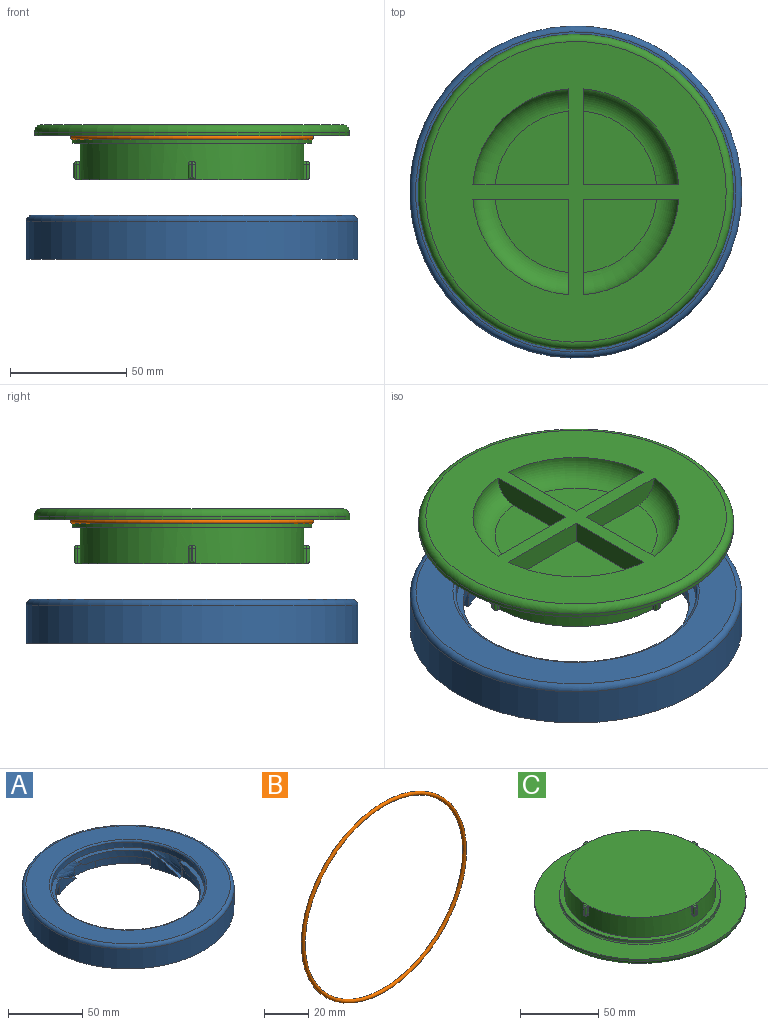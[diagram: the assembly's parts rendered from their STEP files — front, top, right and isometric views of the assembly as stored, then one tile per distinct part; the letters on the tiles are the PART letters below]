
ASSEMBLY  parts=3 mates=2
PART A: 46 faces, bbox 156.1x156.1x20.2 mm
  f0: plane 143.07x143.07mm, normal (0,0,-1), area 7927.9mm2, adj f7,f9,f11,f13,f15,f16,f18,f20
  f1: bspline ~17.63x13.21mm, area 24mm2, adj f10,f11,f17,f40
  f2: bspline ~17.63x13.21mm, area 24mm2, adj f8,f9,f19,f35
  f3: bspline ~17.63x13.21mm, area 24mm2, adj f6,f15,f21,f30
  f4: bspline ~17.63x13.21mm, area 24mm2, adj f5,f7,f23,f25
  f5: plane 46.03x29.1mm, normal (0,0,1), area 168.1mm2, adj f4,f7,f12,f16
  f6: plane 46.03x29.1mm, normal (0,0,1), area 168.1mm2, adj f3,f12,f15,f22
  f7: cylinder r=48.74mm len=48.74mm, axis (0,0,1), area 414.5mm2, adj f0,f4,f5,f16,f25,f28
  f8: plane 46.03x29.1mm, normal (0,0,1), area 168.1mm2, adj f2,f9,f12,f20
  f9: cylinder r=48.74mm len=48.74mm, axis (0,0,1), area 414.5mm2, adj f0,f2,f8,f20,f35,f36
  f10: plane 46.03x29.1mm, normal (0,0,1), area 168.1mm2, adj f1,f11,f12,f18
  f11: cylinder r=48.74mm len=48.74mm, axis (0,0,1), area 414.5mm2, adj f0,f1,f10,f18,f40,f41
  f12: cylinder r=51.82mm len=103.63mm, axis (0,0,-1), area 1447.2mm2, adj f5,f6,f8,f10,f17,f19,f21,f23
  f13: cylinder r=71.53mm len=143.07mm, axis (0,0,-1), area 7363.4mm2, adj f0,f44
  f14: plane 137.99x137.99mm, normal (0,0,1), area 6100.6mm2, adj f44,f45
  f15: cylinder r=48.74mm len=48.74mm, axis (0,0,1), area 414.5mm2, adj f0,f3,f6,f22,f30,f31
  f16: bspline ~24.16x13.21mm, area 56.9mm2, adj f0,f5,f7,f17
  f17: bspline ~41.8x13.21mm, area 183.8mm2, adj f1,f12,f16,f39,f40
  f18: bspline ~24.16x13.21mm, area 56.9mm2, adj f0,f10,f11,f19
  f19: bspline ~41.8x13.21mm, area 183.8mm2, adj f2,f12,f18,f34,f35
  f20: bspline ~24.16x13.21mm, area 56.9mm2, adj f0,f8,f9,f21
  f21: bspline ~41.8x13.21mm, area 183.8mm2, adj f3,f12,f20,f29,f30
  f22: bspline ~24.16x13.21mm, area 56.9mm2, adj f0,f6,f15,f23
  f23: bspline ~41.8x13.21mm, area 183.8mm2, adj f4,f12,f22,f24,f25
  f24: plane 9.07x2.34mm, normal (1,0,0), area 6.6mm2, adj f23,f25,f26
  f25: plane 46.34x30.01mm, normal (0,0,-1), area 155.7mm2, adj f4,f7,f23,f24,f26,f27,f28
  f26: extruded ~17.63x7.82mm, area 140.8mm2, adj f0,f24,f25,f27
  f27: cylinder r=51.82mm len=28.7mm, axis (0,0,-1), area 307.9mm2, adj f0,f25,f26,f28
  f28: plane 7.82x2.75mm, normal (-0.45,0.89,0), area 24.1mm2, adj f0,f7,f25,f27
  f29: plane 9.07x2.34mm, normal (0,1,0), area 6.6mm2, adj f21,f30,f32
  f30: plane 46.34x30.01mm, normal (0,0,-1), area 155.7mm2, adj f3,f15,f21,f29,f31,f32,f33
  f31: plane 7.82x2.75mm, normal (-0.89,-0.45,0), area 24.1mm2, adj f0,f15,f30,f33
  f32: extruded ~17.63x7.82mm, area 140.8mm2, adj f0,f29,f30,f33
  f33: cylinder r=51.82mm len=28.7mm, axis (0,0,-1), area 307.9mm2, adj f0,f30,f31,f32
  f34: plane 9.07x2.34mm, normal (-1,0,0), area 6.6mm2, adj f19,f35,f37
  f35: plane 46.34x30.01mm, normal (0,0,-1), area 155.7mm2, adj f2,f9,f19,f34,f36,f37,f38
  f36: plane 7.82x2.75mm, normal (0.45,-0.89,0), area 24.1mm2, adj f0,f9,f35,f38
  f37: extruded ~17.63x7.82mm, area 140.8mm2, adj f0,f34,f35,f38
  f38: cylinder r=51.82mm len=28.7mm, axis (0,0,-1), area 307.9mm2, adj f0,f35,f36,f37
  f39: plane 9.07x2.34mm, normal (0,-1,0), area 6.6mm2, adj f17,f40,f42
  f40: plane 46.34x30.01mm, normal (0,0,-1), area 155.7mm2, adj f1,f11,f17,f39,f41,f42,f43
  f41: plane 7.82x2.75mm, normal (0.89,0.45,0), area 24.1mm2, adj f0,f11,f40,f43
  f42: extruded ~17.63x7.82mm, area 140.8mm2, adj f0,f39,f40,f43
  f43: cylinder r=51.82mm len=28.7mm, axis (0,0,-1), area 307.9mm2, adj f0,f40,f41,f42
  f44: torus R=68.99mm, axis (0,0,1), area 1770.1mm2, adj f13,f14
  f45: torus R=53.09mm, axis (0,0,1), area 655.3mm2, adj f12,f14
PART B: 1 faces, bbox 113.5x1.8x113.5 mm
  f0: torus R=51.55mm, axis (0,-1,0), area 1809.2mm2
PART C: 80 faces, bbox 147.5x147.5x30.9 mm
  f0: plane 129.54x129.54mm, normal (0,0,-1), area 8060mm2, adj f36,f37,f39,f40,f42,f43,f45,f46
  f1: cylinder r=51.59mm len=103.19mm, axis (0,0,-1), area 514.6mm2, adj f2,f5
  f2: plane 103.19x103.19mm, normal (0,0,1), area 1045.8mm2, adj f1,f4
  f3: plane 96.55x96.55mm, normal (0,0,1), area 7316.9mm2, adj f4,f14,f15,f28,f29
  f4: cylinder r=48.26mm len=96.52mm, axis (0,0,-1), area 4679.5mm2, adj f2,f3,f9,f10,f11,f12,f13,f16
  f5: torus R=51.59mm, axis (0,0,1), area 800.5mm2, adj f1,f7
  f6: cylinder r=67.95mm len=135.89mm, axis (0,0,-1), area 677.7mm2, adj f7,f52
  f7: plane 135.89x135.89mm, normal (0,0,1), area 6140.6mm2, adj f5,f6
  f8: plane 5.29x0.64mm, normal (0,-1,0), area 3.4mm2, adj f71,f74,f75,f76
  f9: plane 6.56x1.3mm, normal (1,0,0), area 8.5mm2, adj f4,f10,f14,f75
  f10: cylinder r=1.27mm len=1.3mm, axis (0,1,0), area 2.6mm2, adj f4,f9,f11,f73
  f11: plane 1.27x0.64mm, normal (0,0,-1), area 0.8mm2, adj f4,f10,f13,f71
  f12: plane 6.56x1.3mm, normal (-1,0,0), area 8.5mm2, adj f4,f13,f14,f74
  f13: cylinder r=1.27mm len=1.3mm, axis (0,1,0), area 2.6mm2, adj f4,f11,f12,f72
  f14: plane 3.19x1.31mm, normal (0,0,1), area 4.1mm2, adj f3,f9,f12,f76
  f15: plane 3.19x1.31mm, normal (0,0,1), area 4.1mm2, adj f3,f19,f20,f70
  f16: cylinder r=1.27mm len=1.3mm, axis (0,1,0), area 2.6mm2, adj f4,f17,f20,f66
  f17: plane 1.27x0.64mm, normal (0,0,-1), area 0.8mm2, adj f4,f16,f18,f65
  f18: cylinder r=1.27mm len=1.3mm, axis (0,1,0), area 2.6mm2, adj f4,f17,f19,f67
  f19: plane 6.56x1.3mm, normal (1,0,0), area 8.5mm2, adj f4,f15,f18,f69
  f20: plane 6.56x1.3mm, normal (-1,0,0), area 8.5mm2, adj f4,f15,f16,f68
  f21: plane 5.29x0.64mm, normal (0,1,0), area 3.4mm2, adj f65,f68,f69,f70
  f22: plane 5.29x0.64mm, normal (1,0,0), area 3.4mm2, adj f59,f62,f63,f64
  f23: plane 6.56x1.3mm, normal (0,1,0), area 8.5mm2, adj f4,f24,f28,f63
  f24: cylinder r=1.27mm len=1.3mm, axis (-1,0,0), area 2.6mm2, adj f4,f23,f25,f61
  f25: plane 1.27x0.64mm, normal (0,0,-1), area 0.8mm2, adj f4,f24,f27,f59
  f26: plane 6.56x1.3mm, normal (0,-1,0), area 8.5mm2, adj f4,f27,f28,f62
  f27: cylinder r=1.27mm len=1.3mm, axis (-1,0,0), area 2.6mm2, adj f4,f25,f26,f60
  f28: plane 3.19x1.31mm, normal (0,0,1), area 4.1mm2, adj f3,f23,f26,f64
  f29: plane 3.19x1.31mm, normal (0,0,1), area 4.1mm2, adj f3,f33,f34,f58
  f30: cylinder r=1.27mm len=1.3mm, axis (-1,0,0), area 2.6mm2, adj f4,f31,f34,f54
  f31: plane 1.27x0.64mm, normal (0,0,-1), area 0.8mm2, adj f4,f30,f32,f53
  f32: cylinder r=1.27mm len=1.3mm, axis (-1,0,0), area 2.6mm2, adj f4,f31,f33,f55
  f33: plane 6.56x1.3mm, normal (0,1,0), area 8.5mm2, adj f4,f29,f32,f57
  f34: plane 6.56x1.3mm, normal (0,-1,0), area 8.5mm2, adj f4,f29,f30,f56
  f35: plane 5.29x0.64mm, normal (-1,0,0), area 3.4mm2, adj f53,f56,f57,f58
  f36: plane 41.58x9.94mm, normal (0,-1,0), area 372.5mm2, adj f0,f37,f38,f51
  f37: plane 41.58x9.94mm, normal (-1,0,0), area 372.5mm2, adj f0,f36,f38,f51
  f38: plane 31.61x31.61mm, normal (0,0,-1), area 746.6mm2, adj f36,f37,f51
  f39: plane 41.58x9.94mm, normal (-1,0,0), area 372.5mm2, adj f0,f40,f41,f50
  f40: plane 41.58x9.94mm, normal (0,1,0), area 372.5mm2, adj f0,f39,f41,f50
  f41: plane 31.61x31.61mm, normal (0,0,-1), area 746.6mm2, adj f39,f40,f50
  f42: plane 41.58x9.94mm, normal (0,1,0), area 372.5mm2, adj f0,f43,f44,f49
  f43: plane 41.58x9.94mm, normal (1,0,0), area 372.5mm2, adj f0,f42,f44,f49
  f44: plane 31.61x31.61mm, normal (0,0,-1), area 746.6mm2, adj f42,f43,f49
  f45: plane 41.58x9.94mm, normal (1,0,0), area 372.5mm2, adj f0,f46,f47,f48
  f46: plane 41.58x9.94mm, normal (0,-1,0), area 372.5mm2, adj f0,f45,f47,f48
  f47: plane 31.61x31.61mm, normal (0,0,-1), area 746.6mm2, adj f45,f46,f48
  f48: torus R=34.92mm, axis (0,0,-1), area 864.1mm2, adj f0,f45,f46,f47
  f49: torus R=34.92mm, axis (0,0,-1), area 864.1mm2, adj f0,f42,f43,f44
  f50: torus R=34.92mm, axis (0,0,-1), area 864.1mm2, adj f0,f39,f40,f41
  f51: torus R=34.92mm, axis (0,0,-1), area 864.1mm2, adj f0,f36,f37,f38
  f52: torus R=64.77mm, axis (0,0,1), area 2093mm2, adj f0,f6
  f53: cylinder r=1.27mm len=1.27mm, axis (0,1,0), area 1.3mm2, adj f31,f35,f54,f55
  f54: sphere r=1.27mm, area 2.5mm2, adj f30,f53,f56
  f55: sphere r=1.27mm, area 1.6mm2, adj f32,f53,f57
  f56: cylinder r=1.27mm len=6.56mm, axis (0,0,-1), area 11.8mm2, adj f34,f35,f54,f58
  f57: cylinder r=1.27mm len=6.56mm, axis (0,0,1), area 11.8mm2, adj f33,f35,f55,f58
  f58: cylinder r=1.27mm len=3.18mm, axis (0,-1,0), area 3.8mm2, adj f29,f35,f56,f57
  f59: cylinder r=1.27mm len=1.27mm, axis (0,-1,0), area 1.3mm2, adj f22,f25,f60,f61
  f60: sphere r=1.27mm, area 2.5mm2, adj f27,f59,f62
  f61: sphere r=1.27mm, area 2.5mm2, adj f24,f59,f63
  f62: cylinder r=1.27mm len=6.56mm, axis (0,0,1), area 11.8mm2, adj f22,f26,f60,f64
  f63: cylinder r=1.27mm len=6.56mm, axis (0,0,-1), area 11.8mm2, adj f22,f23,f61,f64
  f64: cylinder r=1.27mm len=3.18mm, axis (0,1,0), area 3.8mm2, adj f22,f28,f62,f63
  f65: cylinder r=1.27mm len=1.27mm, axis (1,0,0), area 1.3mm2, adj f17,f21,f66,f67
  f66: sphere r=1.27mm, area 2.5mm2, adj f16,f65,f68
  f67: sphere r=1.27mm, area 2.5mm2, adj f18,f65,f69
  f68: cylinder r=1.27mm len=6.56mm, axis (0,0,-1), area 11.8mm2, adj f20,f21,f66,f70
  f69: cylinder r=1.27mm len=6.56mm, axis (0,0,1), area 11.8mm2, adj f19,f21,f67,f70
  f70: cylinder r=1.27mm len=3.18mm, axis (-1,0,0), area 3.8mm2, adj f15,f21,f68,f69
  f71: cylinder r=1.27mm len=1.27mm, axis (-1,0,0), area 1.3mm2, adj f8,f11,f72,f73
  f72: sphere r=1.27mm, area 2.5mm2, adj f13,f71,f74
  f73: sphere r=1.27mm, area 2.5mm2, adj f10,f71,f75
  f74: cylinder r=1.27mm len=6.56mm, axis (0,0,1), area 11.8mm2, adj f8,f12,f72,f76
  f75: cylinder r=1.27mm len=6.56mm, axis (0,0,-1), area 11.8mm2, adj f8,f9,f73,f76
  f76: cylinder r=1.27mm len=3.18mm, axis (1,0,0), area 3.8mm2, adj f8,f14,f74,f75
  f77: cylinder r=45.72mm len=91.44mm, axis (0,0,1), area 2612.2mm2, adj f78,f79
  f78: plane 91.44x91.44mm, normal (0,0,1), area 6566.9mm2, adj f77
  f79: plane 91.44x91.44mm, normal (0,0,-1), area 6566.9mm2, adj f77
PLACE A rot(axis=(1,0,0),0deg) t=(-66.11,9.74,42.87)mm
PLACE B rot(axis=(1,0,0),90deg) t=(-66.11,9.74,95.35)mm
PLACE C rot(axis=(1,0,0),180deg) t=(-66.11,9.74,100.91)mm
MATE slider C.f4 <-> A.f12  axis (0,0,1) through (-66.11,9.74,85.1)mm
MATE revolute B.f0 <-> C.f1  axis (0,0,-1) through (-66.11,9.74,95.35)mm
